# Revit family: Zumtobel CROSSIGN 160 - TEC
name_source: partatom
category: Lighting Fixtures
revit_build: Autodesk Revit 2014 (Build: 20140709_2115(x64)
units: mm (PartAtom-declared; Revit-internal decimal feet)

## types (2) — shared parameters
Apparent Load = 6 VA
Assembly Code = D5020200
Body = Zumtobel_Metal_White
Color Filter = 16777215
Depth = 60 mm  [stored 0.19685 ft]
Description = Escape sign LED luminaire for TECTON track
Dimming Lamp Color Temperature Shift = <None>
ERI = No
Height = 277 mm  [stored 0.908793 ft]
Lamp = LED
Manufacturer = Zumtobel Lighting
Photometric Web File = 42180768+22168595_(STD-LEO).IES
Tilt Angle = 180.00°
URL = http://www.zumtobel.com
Voltage = 230 V
Width = 332 mm  [stored 1.08924 ft]
zero-valued in all types: Default Elevation

## per-type parameters (varying)
| type | Escape Left & Right | Escape Top | Model |
| CROSSIGN 160 TEC LED NT1  + RZ-O | No | Yes | 42183134+22900363 |
| CROSSIGN 160 TEC LED NT1 + RZ-LR | Yes | No | 42183134+22168595/22168596 |

note: [stored X ft] marks values corroborated as IEEE doubles in the binary element streams (Revit-internal decimal feet)

## geometry (parser evidence)
native form markers: Sweep x3
no freeform markers — native parametric forms only
